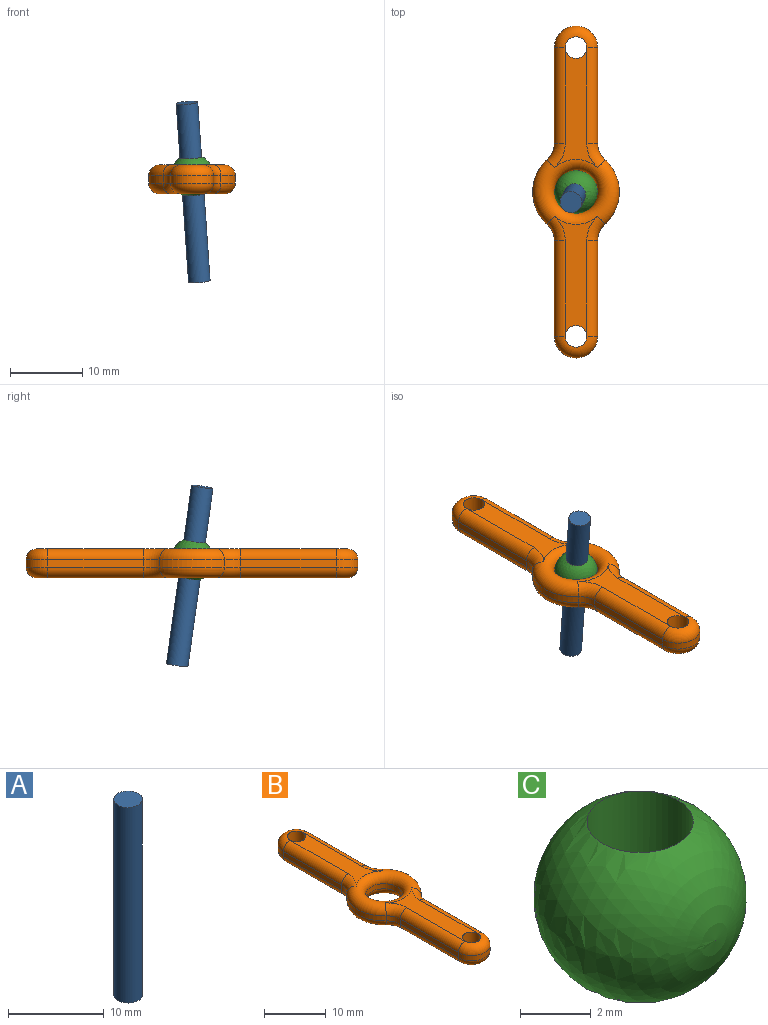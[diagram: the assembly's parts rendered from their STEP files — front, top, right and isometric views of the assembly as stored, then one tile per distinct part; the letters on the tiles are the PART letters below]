
ASSEMBLY  parts=3 mates=2
PART A: 3 faces, bbox 3x3x25 mm
  f0: cylinder r=1.5mm len=25mm, axis (0,0,-1), area 235.6mm2, adj f1,f2
  f1: plane 3x3mm, normal (0,0,1), area 7.1mm2, adj f0
  f2: plane 3x3mm, normal (0,0,-1), area 7.1mm2, adj f0
PART B: 41 faces, bbox 13x46.5x4 mm
  f0: plane 16.65x6mm, normal (0,0,1), area 44.8mm2, adj f16,f33,f35,f37,f39,f40
  f1: plane 16.65x6mm, normal (0,0,-1), area 44.8mm2, adj f16,f23,f24,f26,f28,f29
  f2: cylinder r=3mm len=2.24mm, axis (0,0,-1), area 2.5mm2, adj f3,f15,f25,f36
  f3: plane 13.29x1mm, normal (1,0,0), area 13.3mm2, adj f2,f4,f22,f34
  f4: cylinder r=3mm len=6mm, axis (0,0,-1), area 9.4mm2, adj f3,f5,f20,f32
  f5: plane 13.29x1mm, normal (-1,0,0), area 13.3mm2, adj f4,f6,f19,f30
  f6: cylinder r=3mm len=2.24mm, axis (0,0,-1), area 2.5mm2, adj f5,f7,f21,f31
  f7: cylinder r=6mm len=8.94mm, axis (0,0,-1), area 10.1mm2, adj f6,f8,f23,f33
  f8: cylinder r=3mm len=2.24mm, axis (0,0,-1), area 2.5mm2, adj f7,f9,f24,f35
  f9: plane 13.29x1mm, normal (-1,0,0), area 13.3mm2, adj f8,f10,f26,f37
  f10: cylinder r=3mm len=6mm, axis (0,0,-1), area 9.4mm2, adj f9,f11,f27,f38
  f11: plane 13.29x1mm, normal (1,0,0), area 13.3mm2, adj f10,f12,f29,f40
  f12: cylinder r=3mm len=2.24mm, axis (0,0,-1), area 2.5mm2, adj f11,f15,f28,f39
  f13: cylinder r=1.5mm len=4mm, axis (0,0,-1), area 37.7mm2, adj f17,f18,f20,f32
  f14: cylinder r=3mm len=6mm, axis (0,0,-1), area 18.8mm2, adj f23,f33
  f15: cylinder r=6mm len=8.94mm, axis (0,0,-1), area 10.1mm2, adj f2,f12,f23,f33
  f16: cylinder r=1.5mm len=4mm, axis (0,0,-1), area 37.7mm2, adj f0,f1,f27,f38
  f17: plane 16.65x6mm, normal (0,0,1), area 44.8mm2, adj f13,f30,f31,f33,f34,f36
  f18: plane 16.65x6mm, normal (0,0,-1), area 44.8mm2, adj f13,f19,f21,f22,f23,f25
  f19: cylinder r=1.5mm len=13.29mm, axis (0,-1,0), area 31.3mm2, adj f5,f18,f20,f21
  f20: torus R=1.5mm, axis (0,0,1), area 18.2mm2, adj f4,f13,f19,f22
  f21: torus R=4.5mm, axis (0,0,1), area 7mm2, adj f6,f18,f19,f23
  f22: cylinder r=1.5mm len=13.29mm, axis (0,1,0), area 31.3mm2, adj f3,f18,f20,f25
  f23: torus R=4.5mm, axis (0,0,1), area 95.7mm2, adj f1,f7,f14,f15,f18,f21,f24,f25
  f24: torus R=4.5mm, axis (0,0,1), area 7mm2, adj f1,f8,f23,f26
  f25: torus R=4.5mm, axis (0,0,1), area 7mm2, adj f2,f18,f22,f23
  f26: cylinder r=1.5mm len=13.29mm, axis (0,-1,0), area 31.3mm2, adj f1,f9,f24,f27
  f27: torus R=1.5mm, axis (0,0,1), area 18.2mm2, adj f10,f16,f26,f29
  f28: torus R=4.5mm, axis (0,0,1), area 7mm2, adj f1,f12,f23,f29
  f29: cylinder r=1.5mm len=13.29mm, axis (0,1,0), area 31.3mm2, adj f1,f11,f27,f28
  f30: cylinder r=1.5mm len=13.29mm, axis (0,1,0), area 31.3mm2, adj f5,f17,f31,f32
  f31: torus R=4.5mm, axis (0,0,1), area 7mm2, adj f6,f17,f30,f33
  f32: torus R=1.5mm, axis (0,0,1), area 18.2mm2, adj f4,f13,f30,f34
  f33: torus R=4.5mm, axis (0,0,1), area 95.7mm2, adj f0,f7,f14,f15,f17,f31,f35,f36
  f34: cylinder r=1.5mm len=13.29mm, axis (0,-1,0), area 31.3mm2, adj f3,f17,f32,f36
  f35: torus R=4.5mm, axis (0,0,1), area 7mm2, adj f0,f8,f33,f37
  f36: torus R=4.5mm, axis (0,0,1), area 7mm2, adj f2,f17,f33,f34
  f37: cylinder r=1.5mm len=13.29mm, axis (0,1,0), area 31.3mm2, adj f0,f9,f35,f38
  f38: torus R=1.5mm, axis (0,0,1), area 18.2mm2, adj f10,f16,f37,f40
  f39: torus R=4.5mm, axis (0,0,1), area 7mm2, adj f0,f12,f33,f40
  f40: cylinder r=1.5mm len=13.29mm, axis (0,-1,0), area 31.3mm2, adj f0,f11,f38,f39
PART C: 2 faces, bbox 6x6x6 mm
  f0: sphere r=3mm, area 97.9mm2, adj f1
  f1: cylinder r=1.5mm len=5.2mm, axis (0,0,1), area 49mm2, adj f0
PLACE A rot(axis=(0.15,0.99,0.07),177.3deg) t=(18.32,-7.58,11.05)mm
PLACE B at identity fixed
PLACE C rot(axis=(-0.02,-0.08,1),162.2deg) t=(-19.02,6.16,0.05)mm
MATE slider A.f0 <-> C.f1  axis (-0.07,-0.14,0.99) through (0.16,0.32,-1.75)mm
MATE ball C.f1 <-> B.f7  axis (-0.07,-0.14,0.99) through (0,0,0.5)mm
